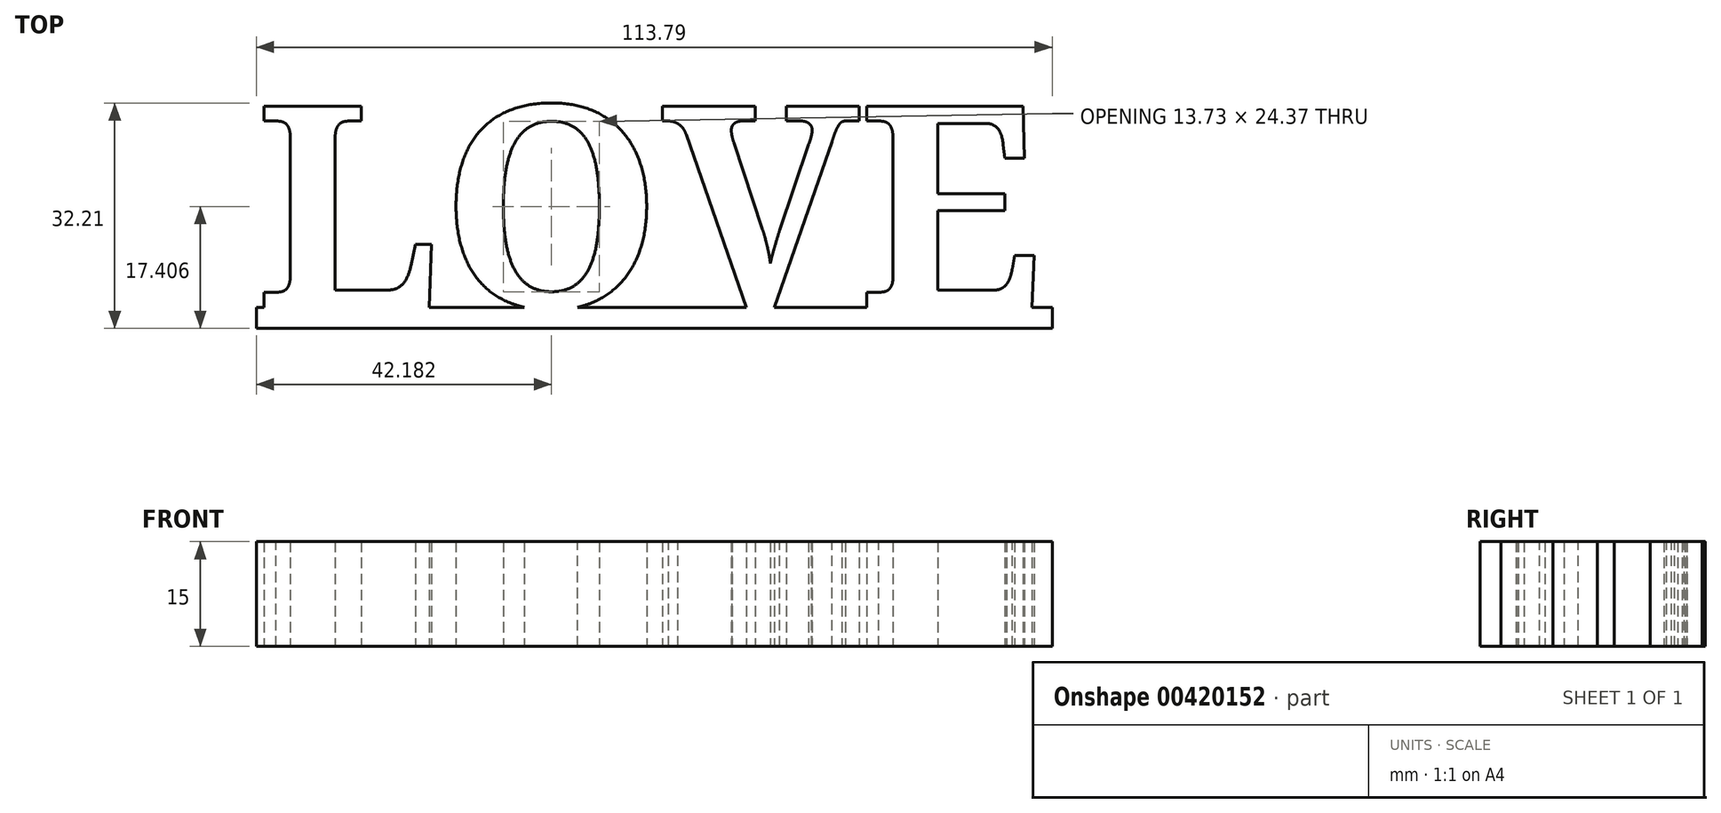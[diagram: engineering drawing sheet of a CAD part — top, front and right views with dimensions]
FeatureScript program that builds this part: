
annotation { "Feature Type Name" : "Feature", "Feature Type Description" : "" }
export const myFeature = defineFeature(function(context is Context, id is Id, definition is map)
    precondition{}
    {
        {
            var Q0;
            Q0=qCreatedBy(makeId("Top.planeOp"),FACE);
            var sketch = newSketch(context, id + "F0", { "sketchPlane" : qUnion([Q0])});
            skText(sketch, "E0", { "text": "LOVE", "fontName": "NotoSerif-Bold.ttf"});
            skLineSegment(sketch, "E1", {"start": v(0, 0) * mm, "end": v(113.8, 0) * mm});
            skLineSegment(sketch, "E2", {"start": v(113.8, 0) * mm, "end": v(113.8, -3) * mm});
            skLineSegment(sketch, "E3", {"start": v(113.8, -3) * mm, "end": v(0, -3) * mm});
            skLineSegment(sketch, "E4", {"start": v(0, -3) * mm, "end": v(0, 0) * mm});
            const initialGuessF0  = {"E0": [0, 0, 1, 0, 0.029]};
            skSetInitialGuess(sketch, initialGuessF0);
            skSolve(sketch);
        }
        {
            var Q0;
            Q0=qSketchRegion(id+"F0",true);
            extrude(context, id + "F1", {"entities" : qUnion([Q0]), "depth" : 15 * mm});
        }
    });
